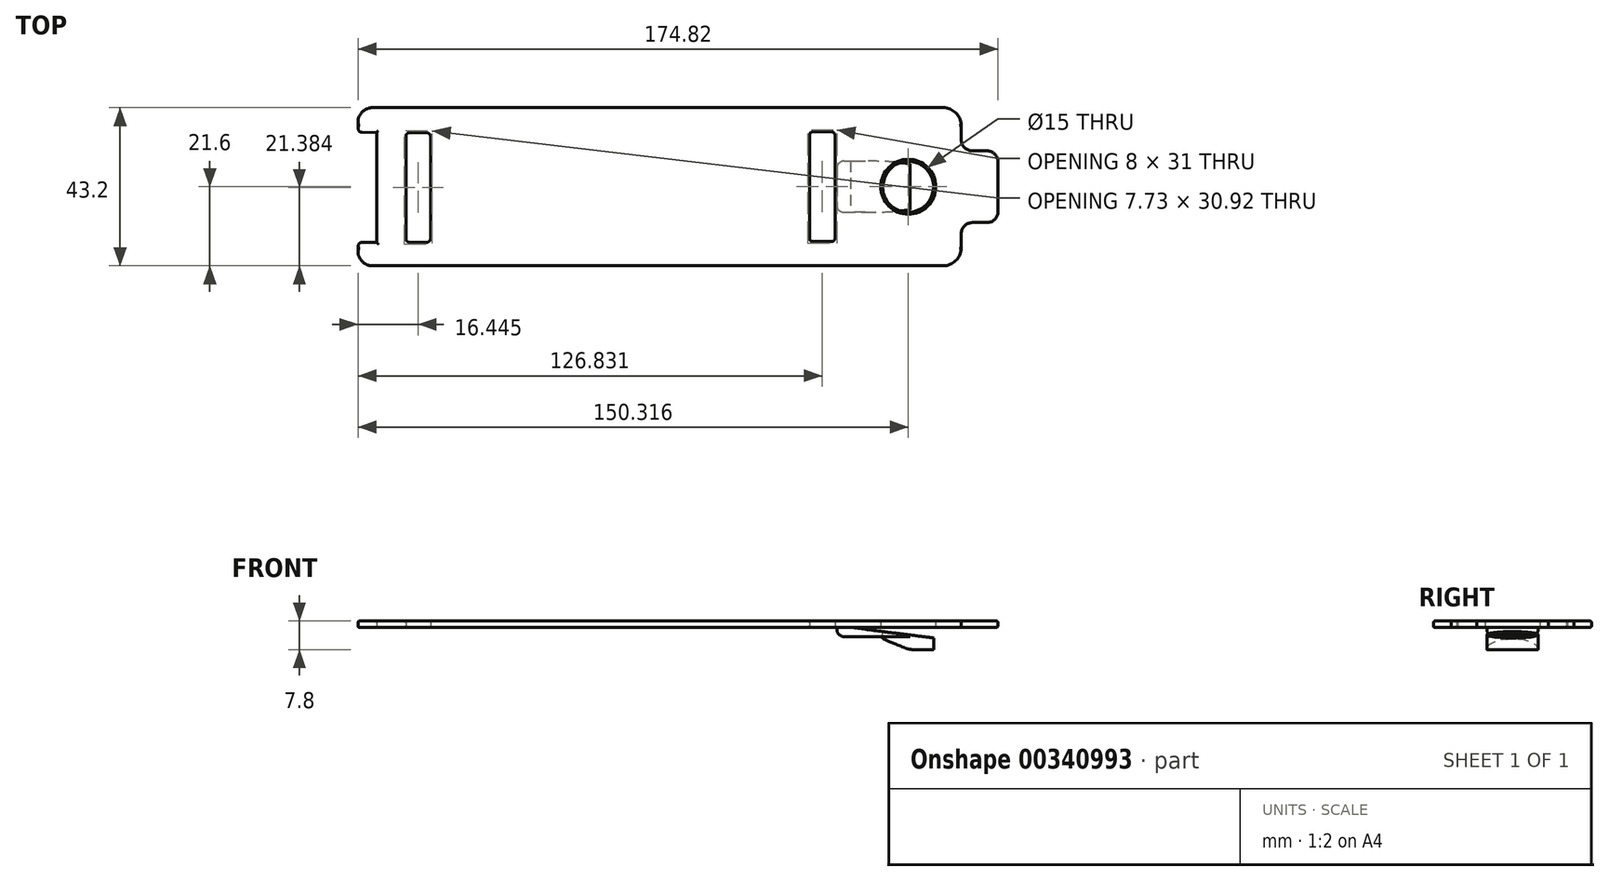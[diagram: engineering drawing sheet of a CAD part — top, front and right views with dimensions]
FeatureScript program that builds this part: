
annotation { "Feature Type Name" : "Feature", "Feature Type Description" : "" }
export const myFeature = defineFeature(function(context is Context, id is Id, definition is map)
    precondition{}
    {
        {
            var Q0;
            Q0=qCreatedBy(makeId("Top.planeOp"),FACE);
            var sketch = newSketch(context, id + "F0", { "sketchPlane" : qUnion([Q0])});
            skLineSegment(sketch, "E0", {"start": v(3.92, 21.6) * mm, "end": v(159.74, 21.6) * mm});
            skPoint(sketch, "E1.visualSharp", {"position": v(-0.26, 21.6) * mm});
            skArc(sketch, "E1.filletArc", {"start": v(3.92, 21.6) * mm, "mid": v(0.83, 20.14) * mm, "end": v(0, 16.82) * mm});
            skPoint(sketch, "E2.visualSharp", {"position": v(164.74, 21.6) * mm});
            skArc(sketch, "E2.filletArc", {"start": v(164.74, 16.8) * mm, "mid": v(163.2, 20.2) * mm, "end": v(159.74, 21.6) * mm});
            skArc(sketch, "E3.MirrorCS", {"start": v(3.92, -21.6) * mm, "mid": v(0.83, -20.14) * mm, "end": v(0, -16.82) * mm});
            skLineSegment(sketch, "E4.MirrorCS", {"start": v(3.92, -21.6) * mm, "end": v(159.74, -21.6) * mm});
            skArc(sketch, "E5.MirrorCS", {"start": v(164.74, -16.8) * mm, "mid": v(163.2, -20.2) * mm, "end": v(159.74, -21.6) * mm});
            skLineSegment(sketch, "E6.top", {"start": v(14, -15.17) * mm, "end": v(18.73, -15.17) * mm});
            skLineSegment(sketch, "E6.left", {"start": v(13, 13.74) * mm, "end": v(13, -14.17) * mm});
            skPoint(sketch, "E7.newPointA", {"position": v(13, 14.83) * mm});
            skArc(sketch, "E7.filletArc", {"start": v(14, 14.74) * mm, "mid": v(13.3, 14.45) * mm, "end": v(13, 13.74) * mm});
            skPoint(sketch, "E8.visualSharp", {"position": v(19.73, -15.17) * mm});
            skArc(sketch, "E8.filletArc", {"start": v(18.73, -15.17) * mm, "mid": v(19.44, -14.88) * mm, "end": v(19.73, -14.17) * mm});
            skPoint(sketch, "E9.visualSharp", {"position": v(13, -15.17) * mm});
            skArc(sketch, "E9.filletArc", {"start": v(13, -14.17) * mm, "mid": v(13.3, -14.88) * mm, "end": v(14, -15.17) * mm});
            skLineSegment(sketch, "E10", {"start": v(0, 16.82) * mm, "end": v(0, 15.85) * mm});
            skLineSegment(sketch, "E11", {"start": v(1, 14.85) * mm, "end": v(5, 14.83) * mm});
            skLineSegment(sketch, "E12", {"start": v(5, 14.83) * mm, "end": v(5, -15.17) * mm});
            skLineSegment(sketch, "E13", {"start": v(5, -15.17) * mm, "end": v(1, -15.17) * mm});
            skLineSegment(sketch, "E14", {"start": v(0, -16.17) * mm, "end": v(0, -16.82) * mm});
            skPoint(sketch, "E15.visualSharp", {"position": v(0, -15.17) * mm});
            skArc(sketch, "E15.filletArc", {"start": v(1, -15.17) * mm, "mid": v(0.3, -15.47) * mm, "end": v(0, -16.17) * mm});
            skPoint(sketch, "E16.visualSharp", {"position": v(0, 14.86) * mm});
            skArc(sketch, "E16.filletArc", {"start": v(0, 15.85) * mm, "mid": v(0.3, 15.15) * mm, "end": v(1, 14.85) * mm});
            skCircle(sketch, "E17", {"center": v(150.24, 0) * mm, "radius": 7.5 * mm});
            skLineSegment(sketch, "E18", {"start": v(130.25, 0) * mm, "end": v(130.25, -14) * mm});
            skLineSegment(sketch, "E19", {"start": v(129.25, -15) * mm, "end": v(124.25, -15) * mm});
            skLineSegment(sketch, "E20", {"start": v(123.25, -14) * mm, "end": v(123.25, 0) * mm});
            skLineSegment(sketch, "E21.MirrorCS", {"start": v(123.25, 14) * mm, "end": v(123.25, 0) * mm});
            skLineSegment(sketch, "E22.MirrorCS", {"start": v(129.25, 15) * mm, "end": v(124.25, 15) * mm});
            skLineSegment(sketch, "E23.MirrorCS", {"start": v(130.25, 0) * mm, "end": v(130.25, 14) * mm});
            skPoint(sketch, "E24.visualSharp", {"position": v(123.25, -15) * mm});
            skArc(sketch, "E24.filletArc", {"start": v(123.25, -14) * mm, "mid": v(123.54, -14.7) * mm, "end": v(124.25, -15) * mm});
            skPoint(sketch, "E25.visualSharp", {"position": v(130.25, -15) * mm});
            skArc(sketch, "E25.filletArc", {"start": v(129.25, -15) * mm, "mid": v(129.96, -14.7) * mm, "end": v(130.25, -14) * mm});
            skPoint(sketch, "E26.visualSharp", {"position": v(123.25, 15) * mm});
            skArc(sketch, "E26.filletArc", {"start": v(124.25, 15) * mm, "mid": v(123.54, 14.7) * mm, "end": v(123.25, 14) * mm});
            skPoint(sketch, "E27.visualSharp", {"position": v(130.25, 15) * mm});
            skArc(sketch, "E27.filletArc", {"start": v(130.25, 14) * mm, "mid": v(129.96, 14.7) * mm, "end": v(129.25, 15) * mm});
            skLineSegment(sketch, "E28", {"start": v(19.73, -14.17) * mm, "end": v(19.73, 13.74) * mm});
            skLineSegment(sketch, "E29", {"start": v(18.73, 14.74) * mm, "end": v(14, 14.74) * mm});
            skPoint(sketch, "E30.visualSharp", {"position": v(19.73, 14.74) * mm});
            skArc(sketch, "E30.filletArc", {"start": v(19.73, 13.74) * mm, "mid": v(19.44, 14.45) * mm, "end": v(18.73, 14.74) * mm});
            skLineSegment(sketch, "E31", {"start": v(164.74, -16.8) * mm, "end": v(164.74, -12.8) * mm});
            skLineSegment(sketch, "E32", {"start": v(167.74, -9.8) * mm, "end": v(171.74, -9.8) * mm});
            skLineSegment(sketch, "E33", {"start": v(174.74, -6.8) * mm, "end": v(174.74, 0) * mm});
            skLineSegment(sketch, "E34.MirrorCS", {"start": v(164.74, 16.8) * mm, "end": v(164.74, 12.8) * mm});
            skLineSegment(sketch, "E35.MirrorCS", {"start": v(167.74, 9.8) * mm, "end": v(171.74, 9.8) * mm});
            skLineSegment(sketch, "E36.MirrorCS", {"start": v(174.74, 6.8) * mm, "end": v(174.74, 0) * mm});
            skPoint(sketch, "E37.visualSharp", {"position": v(164.74, -9.8) * mm});
            skArc(sketch, "E37.filletArc", {"start": v(167.74, -9.8) * mm, "mid": v(165.61, -10.68) * mm, "end": v(164.74, -12.8) * mm});
            skPoint(sketch, "E38.visualSharp", {"position": v(174.74, -9.8) * mm});
            skArc(sketch, "E38.filletArc", {"start": v(171.74, -9.8) * mm, "mid": v(173.86, -8.92) * mm, "end": v(174.74, -6.8) * mm});
            skPoint(sketch, "E39.visualSharp", {"position": v(174.74, 9.8) * mm});
            skArc(sketch, "E39.filletArc", {"start": v(174.74, 6.8) * mm, "mid": v(173.86, 8.92) * mm, "end": v(171.74, 9.8) * mm});
            skPoint(sketch, "E40.visualSharp", {"position": v(164.74, 9.8) * mm});
            skArc(sketch, "E40.filletArc", {"start": v(164.74, 12.8) * mm, "mid": v(165.61, 10.68) * mm, "end": v(167.74, 9.8) * mm});
            skSolve(sketch);
        }
        {
            var Q0;
            Q0=makeQuery(id+"F0.imprint","IMPRINT",FACE,{"disambiguationData":[TD([[makeQuery(id+"F0.imprint","IMPRINT",EDGE,{"derivedFrom":sQuery(id+"F0.wireOp",EDGE,"E0")}),-1.0]])]});
            extrude(context, id + "F1", {"entities" : qUnion([Q0]), "depth" : 1.8 * mm, "offsetDistance" : 25 * mm});
        }
        {
            var Q0;
            Q0=makeQuery(id+"F1.opExtrude","CAP_FACE",FACE,{"disambiguationData":[OSD([sQuery(id+"F0.wireOp",EDGE,"4lImCcik-vaBd-ChDs-FGZK-BXrkIqqKUyUd"),sQuery(id+"F0.wireOp",EDGE,"E0"),sQuery(id+"F0.wireOp",EDGE,"ZmEVUzo8-Rgoz-oXjH-KZA0-teQnxvx4GdeW"),sQuery(id+"F0.wireOp",EDGE,"E1.filletArc"),sQuery(id+"F0.wireOp",EDGE,"E2.filletArc"),sQuery(id+"F0.wireOp",EDGE,"e9c83153-1031-4e30-b199-b86db330d2670.MirrorCS"),sQuery(id+"F0.wireOp",EDGE,"E3.MirrorCS"),sQuery(id+"F0.wireOp",EDGE,"E4.MirrorCS"),sQuery(id+"F0.wireOp",EDGE,"E5.MirrorCS"),sQuery(id+"F0.wireOp",EDGE,"fb28a629-fefc-4467-b64c-ab2c9cce4fbc0.MirrorCS")])],"isStart":false});
            var Q1;
            Q1=makeQuery(id+"F1.opExtrude","CAP_FACE",FACE,{"disambiguationData":[OSD([sQuery(id+"F0.wireOp",EDGE,"4lImCcik-vaBd-ChDs-FGZK-BXrkIqqKUyUd"),sQuery(id+"F0.wireOp",EDGE,"E0"),sQuery(id+"F0.wireOp",EDGE,"ZmEVUzo8-Rgoz-oXjH-KZA0-teQnxvx4GdeW"),sQuery(id+"F0.wireOp",EDGE,"E1.filletArc"),sQuery(id+"F0.wireOp",EDGE,"E2.filletArc"),sQuery(id+"F0.wireOp",EDGE,"e9c83153-1031-4e30-b199-b86db330d2670.MirrorCS"),sQuery(id+"F0.wireOp",EDGE,"E3.MirrorCS"),sQuery(id+"F0.wireOp",EDGE,"E4.MirrorCS"),sQuery(id+"F0.wireOp",EDGE,"E5.MirrorCS"),sQuery(id+"F0.wireOp",EDGE,"fb28a629-fefc-4467-b64c-ab2c9cce4fbc0.MirrorCS")])],"isStart":true});
            fillet(context, id + "F2", {"entities" : qUnion([Q0, Q1]), "radius" : 0.5 * mm, "tangentPropagation" : true, "allowEdgeOverflow" : false});
        }
        {
            var Q0;
            Q0=makeQuery(id+"F1.opExtrude","CAP_FACE",FACE,{"disambiguationData":[OSD([sQuery(id+"F0.wireOp",EDGE,"E0"),sQuery(id+"F0.wireOp",EDGE,"ZmEVUzo8-Rgoz-oXjH-KZA0-teQnxvx4GdeW"),sQuery(id+"F0.wireOp",EDGE,"E1.filletArc"),sQuery(id+"F0.wireOp",EDGE,"E2.filletArc"),sQuery(id+"F0.wireOp",EDGE,"E3.MirrorCS"),sQuery(id+"F0.wireOp",EDGE,"E4.MirrorCS"),sQuery(id+"F0.wireOp",EDGE,"E5.MirrorCS"),sQuery(id+"F0.wireOp",EDGE,"fb28a629-fefc-4467-b64c-ab2c9cce4fbc0.MirrorCS"),sQuery(id+"F0.wireOp",EDGE,"E6.top"),sQuery(id+"F0.wireOp",EDGE,"E6.left"),sQuery(id+"F0.wireOp",EDGE,"E6.right"),sQuery(id+"F0.wireOp",EDGE,"E7.filletArc"),sQuery(id+"F0.wireOp",EDGE,"25758383-3283-4be4-a504-4e04eee22a1a.filletArc"),sQuery(id+"F0.wireOp",EDGE,"E8.filletArc"),sQuery(id+"F0.wireOp",EDGE,"E9.filletArc"),sQuery(id+"F0.wireOp",EDGE,"E10"),sQuery(id+"F0.wireOp",EDGE,"E11"),sQuery(id+"F0.wireOp",EDGE,"E12"),sQuery(id+"F0.wireOp",EDGE,"E13"),sQuery(id+"F0.wireOp",EDGE,"E14"),sQuery(id+"F0.wireOp",EDGE,"E15.filletArc"),sQuery(id+"F0.wireOp",EDGE,"E16.filletArc"),sQuery(id+"F0.wireOp",EDGE,"neuCK5hN-tALS-7sKg-d9Mo-Ycxw4eY6YNgO"),sQuery(id+"F0.wireOp",EDGE,"E17")])],"isStart":true});
            var sketch = newSketch(context, id + "F3", { "sketchPlane" : qUnion([Q0])});
            skCircle(sketch, "E41", {"center": v(150.24, 0) * mm, "radius": 7 * mm});
            skSolve(sketch);
        }
        {
            var Q0;
            Q0=makeQuery(id+"F3.imprint","IMPRINT",FACE,{"disambiguationData":[TD([[makeQuery(id+"F3.imprint","IMPRINT",EDGE,{"derivedFrom":sQuery(id+"F3.wireOp",EDGE,"E41")}),1.0]])]});
            extrude(context, id + "F4", {"entities" : qUnion([Q0]), "depth" : 6 * mm, "offsetDistance" : 25 * mm});
        }
        {
            var Q0;
            Q0=makeQuery(id+"F1.opExtrude","SWEPT_FACE",FACE,{"disambiguationData":[OSD([sQuery(id+"F0.wireOp",EDGE,"E34.MirrorCS")])]});
            var sketch = newSketch(context, id + "F5", { "sketchPlane" : qUnion([Q0])});
            skLineSegment(sketch, "E42", {"start": v(0, 0) * mm, "end": v(-7, 0) * mm});
            skLineSegment(sketch, "E43", {"start": v(-7, 0) * mm, "end": v(-7, -2.5) * mm});
            skLineSegment(sketch, "E44", {"start": v(-7, -2.5) * mm, "end": v(7, -2.5) * mm});
            skLineSegment(sketch, "E45", {"start": v(7, -2.5) * mm, "end": v(7, 0) * mm});
            skLineSegment(sketch, "E46", {"start": v(7, 0) * mm, "end": v(0, 0) * mm});
            skSolve(sketch);
        }
        {
            var Q0;
            Q0=makeQuery(id+"F5.imprint","IMPRINT",FACE,{"disambiguationData":[TD([[makeQuery(id+"F5.imprint","IMPRINT",EDGE,{"derivedFrom":sQuery(id+"F5.wireOp",EDGE,"E42")}),1.0]])]});
            extrude(context, id + "F6", {"entities" : qUnion([Q0]), "oppositeDirection" : true, "depth" : 20 * mm, "offsetDistance" : 25 * mm});
        }
        {
            var Q0;
            Q0=makeQuery(id+"F6.opExtrude","SWEPT_BODY",BODY,{"disambiguationData":[OSD([sQuery(id+"F5.wireOp",EDGE,"E42"),sQuery(id+"F5.wireOp",EDGE,"E43"),sQuery(id+"F5.wireOp",EDGE,"E44"),sQuery(id+"F5.wireOp",EDGE,"E45"),sQuery(id+"F5.wireOp",EDGE,"E46")])]});
            transform(context, id + "F7", {"entities" : qUnion([Q0]), "transformType" : TransformType.TRANSLATION_3D, "dx" : -14 * mm, "dy" : 0 * mm, "dz" : 0 * mm, "makeCopy" : false});
        }
        {
            var Q0;
            Q0=makeQuery(id+"F6.opExtrude","SWEPT_FACE",FACE,{"disambiguationData":[OSD([sQuery(id+"F5.wireOp",EDGE,"E43")])]});
            var sketch = newSketch(context, id + "F8", { "sketchPlane" : qUnion([Q0])});
            skLineSegment(sketch, "E47", {"start": v(157.66, -2.9) * mm, "end": v(157.66, 0) * mm});
            skLineSegment(sketch, "E48", {"start": v(157.66, -2.9) * mm, "end": v(134.48, 0) * mm});
            skLineSegment(sketch, "E49", {"start": v(134.48, 0) * mm, "end": v(157.66, 0) * mm});
            skSolve(sketch);
        }
        {
            var Q0;
            {var subQ0=sQuery(id+"F8.wireOp",EDGE,"E47");Q0=makeQuery(id+"F8.imprint","IMPRINT",FACE,{"disambiguationData":[TD([[makeQuery(id+"F8.imprint","IMPRINT",EDGE,{"derivedFrom":subQ0}),1.0]])]});}
            var Q1;
            {var subQ0=sQuery(id+"F8.wireOp",EDGE,"E49");var subQ2=sQuery(id+"F5.wireOp",EDGE,"E43");var subQ4=makeQuery(id+"F6.opExtrude","CAP_EDGE",EDGE,{"disambiguationData":[OSD([subQ2])],"isStart":true});var subQ6=makeQuery(id+"F8.imprint","INTERSECT",VERTEX,{"derivedFrom":[subQ4,subQ0]});Q1=makeQuery(id+"F8.imprint","IMPRINT",FACE,{"disambiguationData":[TD([[makeQuery(id+"F8.imprint","IMPRINT",EDGE,{"disambiguationData":[TD([[subQ6,-1.0]])],"derivedFrom":subQ4}),-1.0]])]});}
            extrude(context, id + "F9", {"entities" : qUnion([Q0, Q1]), "oppositeDirection" : true, "depth" : 25 * mm, "offsetDistance" : 25 * mm});
        }
        {
            var Q0;
            Q0=makeQuery(id+"F9.opExtrude","SWEPT_BODY",BODY,{"disambiguationData":[OSD([sQuery(id+"F8.wireOp",EDGE,"E47"),sQuery(id+"F8.wireOp",EDGE,"E48"),sQuery(id+"F8.wireOp",EDGE,"E49")])]});
            var Q1;
            Q1=makeQuery(id+"F4.opExtrude","SWEPT_BODY",BODY,{"disambiguationData":[OSD([sQuery(id+"F3.wireOp",EDGE,"E41")])]});
            var Q2;
            Q2=makeQuery(id+"F6.opExtrude","SWEPT_BODY",BODY,{"disambiguationData":[OSD([sQuery(id+"F5.wireOp",EDGE,"E42"),sQuery(id+"F5.wireOp",EDGE,"E43"),sQuery(id+"F5.wireOp",EDGE,"E44"),sQuery(id+"F5.wireOp",EDGE,"E45"),sQuery(id+"F5.wireOp",EDGE,"E46")])]});
            booleanBodies(context, id + "F10", {"operationType" : BooleanOperationType.SUBTRACTION, "tools" : qUnion([Q0]), "targets" : qUnion([Q1, Q2])});
        }
        {
            var Q0;
            Q0=makeQuery(id+"F6.opExtrude","CAP_EDGE",EDGE,{"disambiguationData":[OSD([sQuery(id+"F5.wireOp",EDGE,"E45")])],"isStart":false});
            var Q1;
            Q1=makeQuery(id+"F6.opExtrude","CAP_EDGE",EDGE,{"disambiguationData":[OSD([sQuery(id+"F5.wireOp",EDGE,"E43")])],"isStart":false});
            var Q2;
            Q2=makeQuery(id+"F6.opExtrude","CAP_EDGE",EDGE,{"disambiguationData":[OSD([sQuery(id+"F5.wireOp",EDGE,"E44")])],"isStart":false});
            var Q3;
            Q3=makeQuery(id+"F6.opExtrude","SWEPT_EDGE",EDGE,{"disambiguationData":[OSD([sQuery(id+"F5.wireOp",EDGE,"E43"),sQuery(id+"F5.wireOp",EDGE,"E44")])]});
            var Q4;
            Q4=makeQuery(id+"F6.opExtrude","SWEPT_EDGE",EDGE,{"disambiguationData":[OSD([sQuery(id+"F5.wireOp",EDGE,"E44"),sQuery(id+"F5.wireOp",EDGE,"E45")])]});
            fillet(context, id + "F11", {"entities" : qUnion([Q0, Q1, Q2, Q3, Q4]), "radius" : 2 * mm, "tangentPropagation" : true, "allowEdgeOverflow" : false});
        }
        {
            var Q0;
            Q0=makeQuery(id+"F1.opExtrude","SWEPT_FACE",FACE,{"disambiguationData":[OSD([sQuery(id+"F0.wireOp",EDGE,"E4.MirrorCS")])]});
            var sketch = newSketch(context, id + "F12", { "sketchPlane" : qUnion([Q0])});
            skLineSegment(sketch, "E50", {"start": v(143.18, -3) * mm, "end": v(150.65, -6.1) * mm});
            skLineSegment(sketch, "E51", {"start": v(150.65, -6.1) * mm, "end": v(143.18, -6.1) * mm});
            skLineSegment(sketch, "E52", {"start": v(143.18, -6.1) * mm, "end": v(143.18, -3) * mm});
            skSolve(sketch);
        }
        {
            var Q0;
            Q0=makeQuery(id+"F12.imprint","IMPRINT",FACE,{"disambiguationData":[TD([[makeQuery(id+"F12.imprint","IMPRINT",EDGE,{"derivedFrom":sQuery(id+"F12.wireOp",EDGE,"E50")}),-1.0]])]});
            extrude(context, id + "F13", {"entities" : qUnion([Q0]), "operationType" : NewBodyOperationType.REMOVE, "oppositeDirection" : true, "depth" : 30 * mm, "offsetDistance" : 25 * mm});
        }
        {
            var Q0;
            Q0=makeQuery(id+"F13.boolean.opBoolean","INTERSECT",EDGE,{"derivedFrom":[makeQuery(id+"F4.opExtrude","CAP_FACE",FACE,{"disambiguationData":[OSD([sQuery(id+"F3.wireOp",EDGE,"E41")])],"isStart":false}),makeQuery(id+"F13.opExtrude","SWEPT_FACE",FACE,{"disambiguationData":[OSD([sQuery(id+"F12.wireOp",EDGE,"E50")])]})]});
            fillet(context, id + "F14", {"entities" : qUnion([Q0]), "radius" : 5 * mm, "tangentPropagation" : true, "allowEdgeOverflow" : false});
        }
    });
